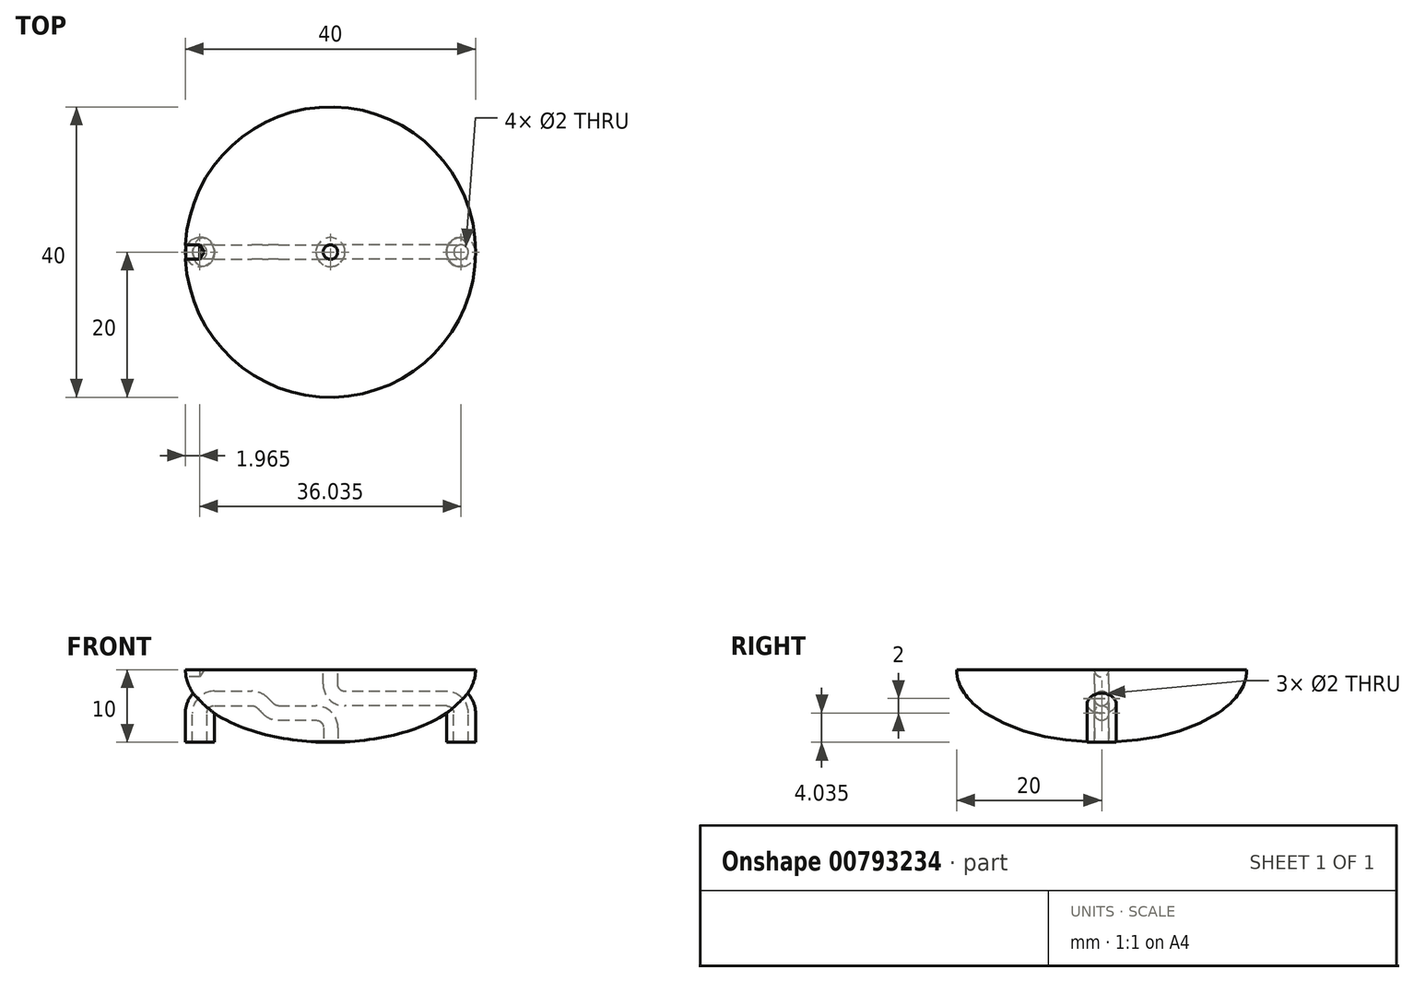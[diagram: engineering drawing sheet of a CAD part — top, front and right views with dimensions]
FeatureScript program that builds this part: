
annotation { "Feature Type Name" : "Feature", "Feature Type Description" : "" }
export const myFeature = defineFeature(function(context is Context, id is Id, definition is map)
    precondition{}
    {
        {
            var Q0;
            Q0=qCreatedBy(makeId("Front.planeOp"),FACE);
            var sketch = newSketch(context, id + "F0", { "sketchPlane" : qUnion([Q0])});
            skEllipticalArc(sketch, "E0", {});
            skEllipticalArc(sketch, "E1", {});
            skFitSpline(sketch, "E2.0", {"points": [v(18.6, -1.5) * mm, v(18.9, 0) * mm, v(18.6, 1.5) * mm, v(17.83, 2.8) * mm, v(16.85, 3.84) * mm, v(15.63, 4.86) * mm, v(13.7, 6.04) * mm, v(11.3, 7.02) * mm, v(9.13, 7.67) * mm, v(6.85, 8.21) * mm, v(4.42, 8.58) * mm, v(1.91, 8.77) * mm, v(0, 8.82) * mm, v(-1.91, 8.77) * mm, v(-4.42, 8.58) * mm, v(-6.85, 8.21) * mm, v(-9.13, 7.67) * mm, v(-11.3, 7.02) * mm, v(-13.7, 6.04) * mm, v(-15.63, 4.86) * mm, v(-16.85, 3.84) * mm, v(-17.83, 2.8) * mm, v(-18.6, 1.5) * mm, v(-18.9, 0) * mm, v(-18.6, -1.5) * mm, v(-17.83, -2.8) * mm, v(-16.85, -3.84) * mm, v(-15.63, -4.86) * mm, v(-13.7, -6.04) * mm, v(-11.3, -7.02) * mm, v(-9.13, -7.67) * mm, v(-6.85, -8.21) * mm, v(-4.42, -8.58) * mm, v(-1.91, -8.77) * mm, v(0, -8.82) * mm, v(1.91, -8.77) * mm, v(4.42, -8.58) * mm, v(6.85, -8.21) * mm, v(9.13, -7.67) * mm, v(11.3, -7.02) * mm, v(13.7, -6.04) * mm, v(15.63, -4.86) * mm, v(16.85, -3.84) * mm, v(17.83, -2.8) * mm, v(18.6, -1.5) * mm, v(18.9, 0) * mm, v(18.6, 1.5) * mm]});
            skLineSegment(sketch, "E3", {"start": v(0, 10) * mm, "end": v(0, 8.8) * mm});
            skLineSegment(sketch, "E4", {"start": v(-20, 0) * mm, "end": v(0, 0) * mm});
            skLineSegment(sketch, "E5", {"start": v(0, 0) * mm, "end": v(0, -10) * mm});
            const initialGuessF0  = {"E0": [0, 0, 1, 0, 0.02, 0.01, 1.5707963267948966, 3.141592653589793], "E1": [0, 0, 1, 0, 0.02, 0.01, 3.141592653589793, 4.71238898038469]};
            skSetInitialGuess(sketch, initialGuessF0);
            skSolve(sketch);
        }
        {
            var Q0;
            Q0=qCreatedBy(makeId("Top.planeOp"),FACE);
            cPlane(context, id + "F1", {"entities" : qUnion([Q0]), "cplaneType" : CPlaneType.OFFSET, "offset" : 10 * mm, "oppositeDirection" : true, "width" : 150 * mm, "height" : 150 * mm});
        }
        {
            var Q0;
            Q0 = qSketchRegion(id + "F0", true);
            var Q1;
            Q1=sQuery(id+"F0.wireOp",EDGE,"E5");
            revolve(context, id + "F2", {"surfaceOperationType" : NewSurfaceOperationType.NEW, "entities" : qUnion([Q0]), "axis" : qUnion([Q1]), "revolveType" : RevolveType.FULL});
        }
        {
            var Q0;
            Q0=qCreatedBy(makeId("Front.planeOp"),FACE);
            var sketch = newSketch(context, id + "F3", { "sketchPlane" : qUnion([Q0])});
            skPoint(sketch, "E6.newPointA", {"position": v(-18, 9.91) * mm});
            skPoint(sketch, "E7.newPointB", {"position": v(0, 11.28) * mm});
            skLineSegment(sketch, "E8", {"start": v(-24.7, 0) * mm, "end": v(25.04, 0) * mm, "construction": true});
            skPoint(sketch, "E9.visualSharp", {"position": v(0, -4) * mm});
            skLineSegment(sketch, "E10", {"start": v(-18, -6) * mm, "end": v(-18, -6) * mm});
            skLineSegment(sketch, "E11", {"start": v(-9.41, -4.59) * mm, "end": v(-9, -5) * mm});
            skLineSegment(sketch, "E12", {"start": v(-9, -5) * mm, "end": v(-8.59, -5.41) * mm});
            skLineSegment(sketch, "E13", {"start": v(-7.17, -6) * mm, "end": v(-2, -6) * mm});
            skPoint(sketch, "E14.visualSharp", {"position": v(-10, -4) * mm});
            skArc(sketch, "E14.filletArc", {"start": v(-9.41, -4.59) * mm, "mid": v(-10.06, -4.15) * mm, "end": v(-10.83, -4) * mm});
            skPoint(sketch, "E15.visualSharp", {"position": v(-8, -6) * mm});
            skArc(sketch, "E15.filletArc", {"start": v(-8.59, -5.41) * mm, "mid": v(-7.94, -5.85) * mm, "end": v(-7.17, -6) * mm});
            skPoint(sketch, "E16.newPointB", {"position": v(0, 16.57) * mm});
            skArc(sketch, "E16.filletArc", {"start": v(0, -8) * mm, "mid": v(-0.59, -6.59) * mm, "end": v(-2, -6) * mm});
            skLineSegment(sketch, "E17", {"start": v(0, -8) * mm, "end": v(0, -10) * mm});
            skLineSegment(sketch, "E18", {"start": v(6.87, -10) * mm, "end": v(-20.7, -10) * mm, "construction": true});
            skLineSegment(sketch, "E19", {"start": v(-18, -10) * mm, "end": v(-18, -6) * mm});
            skLineSegment(sketch, "E20", {"start": v(-16, -4) * mm, "end": v(-10.83, -4) * mm});
            skPoint(sketch, "E21.visualSharp", {"position": v(-18, -4) * mm});
            skArc(sketch, "E21.filletArc", {"start": v(-16, -4) * mm, "mid": v(-17.41, -4.59) * mm, "end": v(-18, -6) * mm});
            skSolve(sketch);
        }
        {
            var Q0;
            Q0=qCreatedBy(id+"F1.planeOp",FACE);
            var sketch = newSketch(context, id + "F4", { "sketchPlane" : qUnion([Q0])});
            skCircle(sketch, "E22", {"center": v(-18, 0) * mm, "radius": 2 * mm});
            skSolve(sketch);
        }
        {
            var Q0;
            Q0 = qSketchRegion(id + "F4", true);
            var Q1;
            Q1 = qConstructionFilter(qBodyType(qCreatedBy(id + "F3" ,EDGE), BodyType.WIRE), ConstructionObject.NO);
            sweep(context, id + "F5", {"operationType" : NewBodyOperationType.ADD, "profiles" : qUnion([Q0]), "path" : qUnion([Q1])});
        }
        {
            var Q0;
            Q0=qCreatedBy(id+"F1.planeOp",FACE);
            var sketch = newSketch(context, id + "F6", { "sketchPlane" : qUnion([Q0])});
            skCircle(sketch, "E23", {"center": v(-18.03, 0) * mm, "radius": 1 * mm});
            skSolve(sketch);
        }
        {
            var Q0;
            Q0=makeQuery(id+"F6.imprint","IMPRINT",FACE,{"disambiguationData":[TD([[makeQuery(id+"F6.imprint","IMPRINT",EDGE,{"derivedFrom":sQuery(id+"F6.wireOp",EDGE,"E23")}),1.0]])]});
            var Q1;
            Q1 = qConstructionFilter(qBodyType(qCreatedBy(id + "F3" ,EDGE), BodyType.WIRE), ConstructionObject.NO);
            sweep(context, id + "F7", {"operationType" : NewBodyOperationType.REMOVE, "profiles" : qUnion([Q0]), "path" : qUnion([Q1])});
        }
        {
            var Q0;
            Q0=qCreatedBy(makeId("Front.planeOp"),FACE);
            var sketch = newSketch(context, id + "F8", { "sketchPlane" : qUnion([Q0])});
            skPoint(sketch, "E24.newPointA", {"position": v(24.92, -4) * mm});
            skLineSegment(sketch, "E25", {"start": v(18, -4) * mm, "end": v(18, -4) * mm});
            skLineSegment(sketch, "E26", {"start": v(0, 0) * mm, "end": v(0, 0) * mm});
            skPoint(sketch, "E27.visualSharp", {"position": v(18, -4) * mm});
            skArc(sketch, "E27.filletArc", {"start": v(18, -6) * mm, "mid": v(17.41, -4.59) * mm, "end": v(16, -4) * mm});
            skLineSegment(sketch, "E28", {"start": v(18, -6) * mm, "end": v(18, -10) * mm});
            skLineSegment(sketch, "E29", {"start": v(16, -4) * mm, "end": v(11, -4) * mm});
            skLineSegment(sketch, "E30", {"start": v(0, 0) * mm, "end": v(0, -2) * mm});
            skLineSegment(sketch, "E31", {"start": v(2, -4) * mm, "end": v(11, -4) * mm});
            skPoint(sketch, "E32.visualSharp", {"position": v(0, -4) * mm});
            skArc(sketch, "E32.filletArc", {"start": v(0, -2) * mm, "mid": v(0.59, -3.41) * mm, "end": v(2, -4) * mm});
            skSolve(sketch);
        }
        {
            var Q0;
            Q0=qCreatedBy(id+"F1.planeOp",FACE);
            var sketch = newSketch(context, id + "F9", { "sketchPlane" : qUnion([Q0])});
            skCircle(sketch, "E33", {"center": v(18, 0) * mm, "radius": 2 * mm});
            skSolve(sketch);
        }
        {
            var Q0;
            Q0 = qSketchRegion(id + "F9", true);
            var Q1;
            Q1 = qConstructionFilter(qBodyType(qCreatedBy(id + "F8" ,EDGE), BodyType.WIRE), ConstructionObject.NO);
            sweep(context, id + "F10", {"operationType" : NewBodyOperationType.ADD, "profiles" : qUnion([Q0]), "path" : qUnion([Q1])});
        }
        {
            var Q0;
            Q0=qCreatedBy(id+"F1.planeOp",FACE);
            var sketch = newSketch(context, id + "F11", { "sketchPlane" : qUnion([Q0])});
            skCircle(sketch, "E34", {"center": v(18, 0) * mm, "radius": 1 * mm});
            skSolve(sketch);
        }
        {
            var Q0;
            Q0 = qSketchRegion(id + "F11", true);
            var Q1;
            Q1 = qConstructionFilter(qBodyType(qCreatedBy(id + "F8" ,EDGE), BodyType.WIRE), ConstructionObject.NO);
            sweep(context, id + "F12", {"operationType" : NewBodyOperationType.REMOVE, "profiles" : qUnion([Q0]), "path" : qUnion([Q1])});
        }
        {
            var Q0;
            Q0=qCreatedBy(makeId("Right.planeOp"),FACE);
            cPlane(context, id + "F13", {"entities" : qUnion([Q0]), "cplaneType" : CPlaneType.OFFSET, "offset" : 20 * mm, "oppositeDirection" : true, "width" : 150 * mm, "height" : 150 * mm});
        }
        {
            var Q0;
            Q0=qCreatedBy(id+"F13.planeOp",FACE);
            var sketch = newSketch(context, id + "F14", { "sketchPlane" : qUnion([Q0])});
            skPoint(sketch, "E35", {"position": v(0, 0) * mm});
            skSolve(sketch);
        }
        {
            var Q0;
            Q0=sQuery(id+"F14.wireOp",VERTEX,"E35");
            var Q1;
            Q1=makeQuery(id+"F2.opRevolve","SWEPT_BODY",BODY,{"disambiguationData":[OSD([sQuery(id+"F0.wireOp",EDGE,"E0"),sQuery(id+"F0.wireOp",EDGE,"E1"),sQuery(id+"F0.wireOp",EDGE,"E2.0"),sQuery(id+"F0.wireOp",EDGE,"E3"),sQuery(id+"F0.wireOp",EDGE,"E4"),sQuery(id+"F0.wireOp",EDGE,"E5")])]});
            hole(context, id + "F15", {"style" : HoleStyle.SIMPLE, "endStyle" : HoleEndStyle.BLIND, "oppositeDirection" : true, "holeDiameter" : 2 * mm, "majorDiameter" : 5 * mm, "holeDepth" : 2 * mm, "isTappedThrough" : true, "tappedDepth" : 12 * mm, "tapClearance" : 3, "locations" : qUnion([Q0]), "scope" : qUnion([Q1])});
        }
    });
